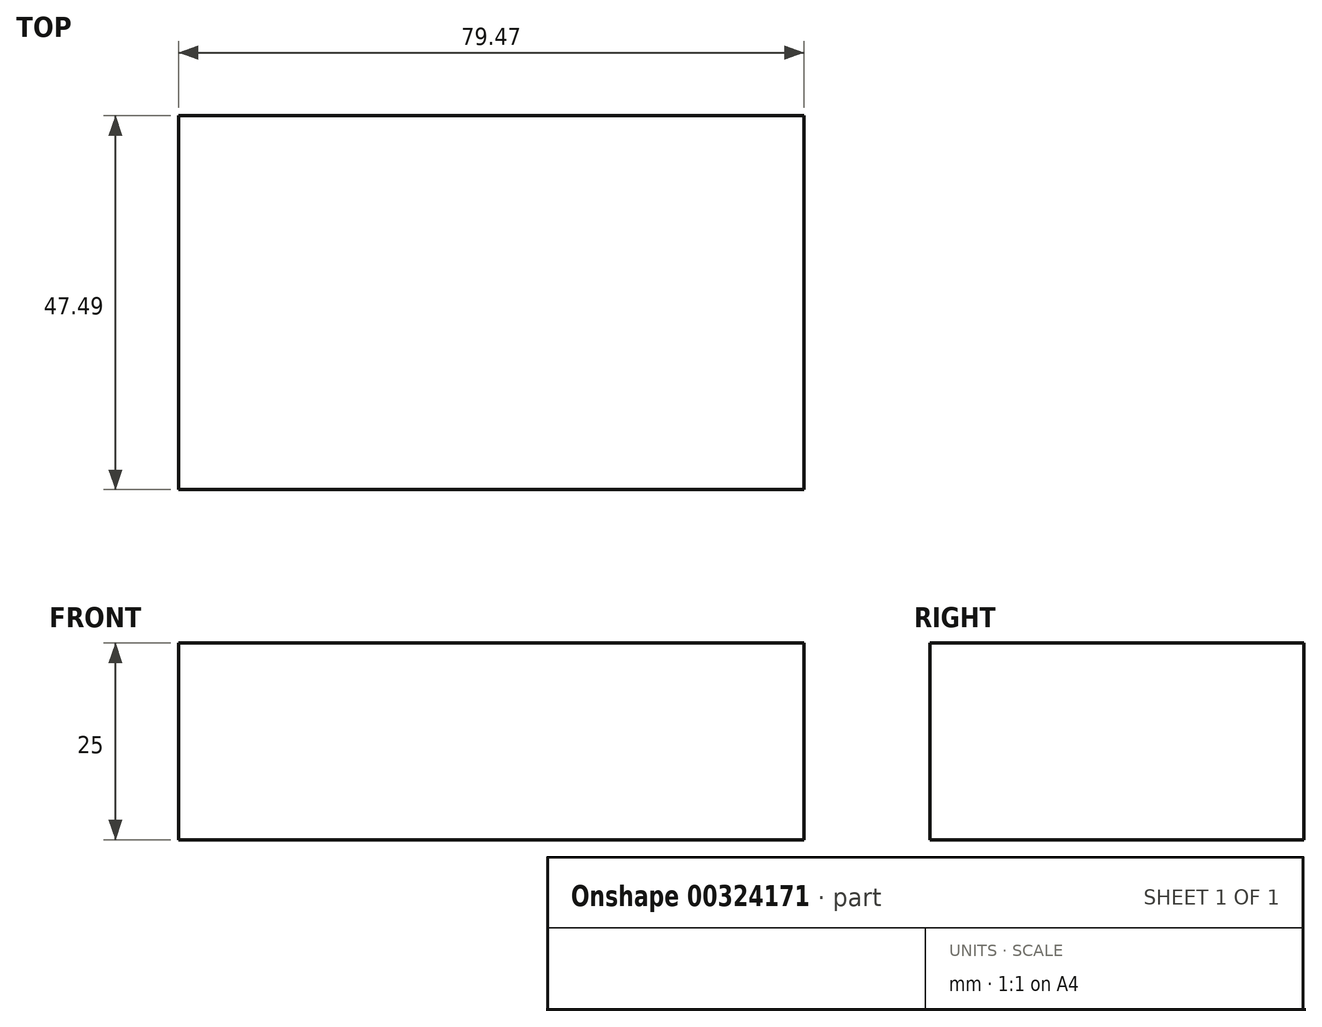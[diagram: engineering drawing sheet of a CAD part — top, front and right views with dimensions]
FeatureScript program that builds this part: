
annotation { "Feature Type Name" : "Feature", "Feature Type Description" : "" }
export const myFeature = defineFeature(function(context is Context, id is Id, definition is map)
    precondition{}
    {
        {
            var Q0;
            Q0=qCreatedBy(makeId("Top.planeOp"),FACE);
            var sketch = newSketch(context, id + "F0", { "sketchPlane" : qUnion([Q0])});
            skLineSegment(sketch, "E0.bottom", {"start": v(-45.88, 25.56) * mm, "end": v(33.59, 25.56) * mm});
            skLineSegment(sketch, "E0.top", {"start": v(-45.88, -21.93) * mm, "end": v(33.59, -21.93) * mm});
            skLineSegment(sketch, "E0.left", {"start": v(-45.88, 25.56) * mm, "end": v(-45.88, -21.93) * mm});
            skLineSegment(sketch, "E0.right", {"start": v(33.59, 25.56) * mm, "end": v(33.59, -21.93) * mm});
            skSolve(sketch);
        }
        {
            var Q0;
            Q0=makeQuery(id+"F0.imprint","IMPRINT",FACE,{"disambiguationData":[TD([[makeQuery(id+"F0.imprint","IMPRINT",EDGE,{"derivedFrom":sQuery(id+"F0.wireOp",EDGE,"E0.bottom")}),-1.0]])]});
            extrude(context, id + "F1", {"entities" : qUnion([Q0]), "depth" : 25 * mm});
        }
    });
